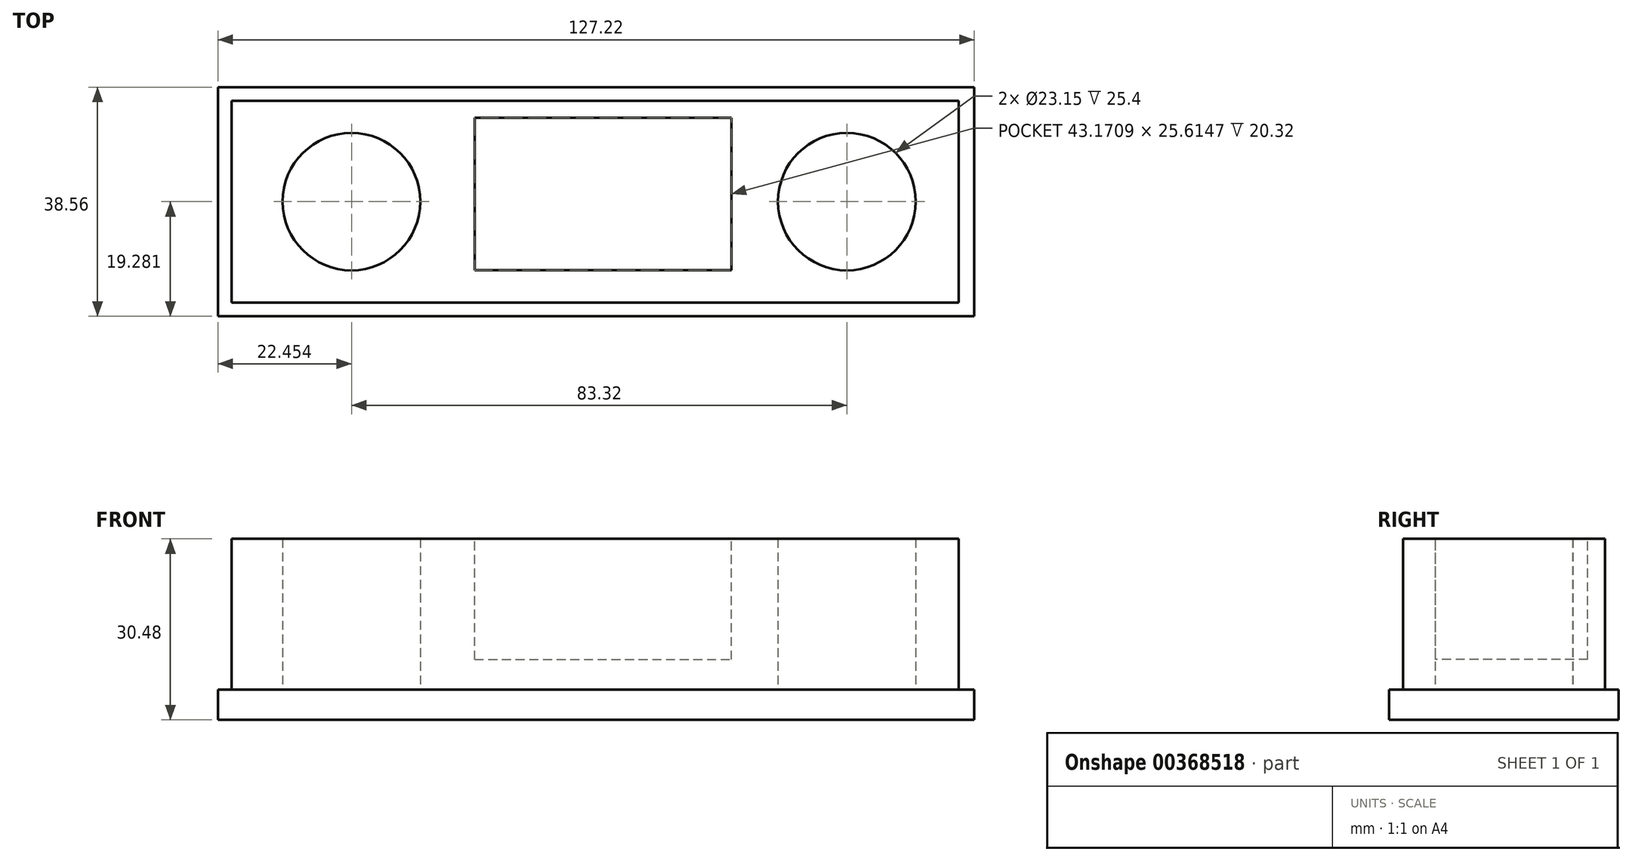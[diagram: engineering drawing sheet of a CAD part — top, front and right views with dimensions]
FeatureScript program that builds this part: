
annotation { "Feature Type Name" : "Feature", "Feature Type Description" : "" }
export const myFeature = defineFeature(function(context is Context, id is Id, definition is map)
    precondition{}
    {
        {
            var Q0;
            Q0=qCreatedBy(makeId("Top.planeOp"),FACE);
            var sketch = newSketch(context, id + "F0", { "sketchPlane" : qUnion([Q0])});
            skLineSegment(sketch, "E0.bottom", {"start": v(-63.6, 41.44) * mm, "end": v(63.6, 41.44) * mm});
            skLineSegment(sketch, "E0.top", {"start": v(-63.6, 2.88) * mm, "end": v(63.6, 2.88) * mm});
            skLineSegment(sketch, "E0.left", {"start": v(-63.6, 41.44) * mm, "end": v(-63.6, 2.88) * mm});
            skLineSegment(sketch, "E0.right", {"start": v(63.6, 41.44) * mm, "end": v(63.6, 2.88) * mm});
            skSolve(sketch);
        }
        {
            var Q0;
            Q0 = qSketchRegion(id + "F0", true);
            var Q1;
            Q1=makeQuery(id+"F0.imprint","IMPRINT",FACE,{"disambiguationData":[TD([[makeQuery(id+"F0.imprint","IMPRINT",EDGE,{"derivedFrom":sQuery(id+"F0.wireOp",EDGE,"E0.bottom")}),-1.0]])]});
            extrude(context, id + "F1", {"entities" : qUnion([Q0, Q1]), "oppositeDirection" : true, "depth" : 5.08 * mm});
        }
        {
            var Q0;
            Q0=makeQuery(id+"F1.opExtrude","CAP_FACE",FACE,{"disambiguationData":[OSD([sQuery(id+"F0.wireOp",EDGE,"E0.bottom"),sQuery(id+"F0.wireOp",EDGE,"E0.top"),sQuery(id+"F0.wireOp",EDGE,"E0.left"),sQuery(id+"F0.wireOp",EDGE,"E0.right")])],"isStart":true});
            var sketch = newSketch(context, id + "F2", { "sketchPlane" : qUnion([Q0])});
            skLineSegment(sketch, "E1.left", {"start": v(-61.3, 39.14) * mm, "end": v(-61.3, 5.18) * mm});
            skLineSegment(sketch, "E1.right", {"start": v(61.01, 39.14) * mm, "end": v(61.01, 5.18) * mm});
            skLineSegment(sketch, "E2.bottom", {"start": v(-63.6, 41.44) * mm, "end": v(-0.14, 41.44) * mm});
            skLineSegment(sketch, "E2.top", {"start": v(-63.6, 2.88) * mm, "end": v(-0.14, 2.88) * mm});
            skLineSegment(sketch, "E2.left", {"start": v(-63.6, 41.44) * mm, "end": v(-63.6, 2.88) * mm});
            skCircle(sketch, "E3", {"center": v(-41.16, 22.16) * mm, "radius": 11.58 * mm});
            skCircle(sketch, "E4", {"center": v(42.16, 22.16) * mm, "radius": 11.57 * mm});
            skLineSegment(sketch, "E5", {"start": v(-61.3, 39.14) * mm, "end": v(61.01, 39.14) * mm});
            skLineSegment(sketch, "E6", {"start": v(-61.3, 5.18) * mm, "end": v(61.01, 5.18) * mm});
            skSolve(sketch);
        }
        {
            var Q0;
            Q0=makeQuery(id+"F2.imprint","IMPRINT",FACE,{"disambiguationData":[TD([[makeQuery(id+"F2.imprint","IMPRINT",EDGE,{"derivedFrom":sQuery(id+"F2.wireOp",EDGE,"E1.left")}),1.0]])]});
            extrude(context, id + "F3", {"entities" : qUnion([Q0]), "operationType" : NewBodyOperationType.ADD, "depth" : 25.4 * mm});
        }
        {
            var Q0;
            Q0=makeQuery(id+"F3.opExtrude","CAP_FACE",FACE,{"disambiguationData":[OSD([sQuery(id+"F2.wireOp",EDGE,"E1.left"),sQuery(id+"F2.wireOp",EDGE,"E1.right"),sQuery(id+"F2.wireOp",EDGE,"E3"),sQuery(id+"F2.wireOp",EDGE,"E4"),sQuery(id+"F2.wireOp",EDGE,"E5"),sQuery(id+"F2.wireOp",EDGE,"E6")])],"isStart":false});
            var sketch = newSketch(context, id + "F4", { "sketchPlane" : qUnion([Q0])});
            skLineSegment(sketch, "E7.bottom", {"start": v(-0.14, 39.14) * mm, "end": v(21.59, 39.14) * mm});
            skLineSegment(sketch, "E7.top", {"start": v(-0.14, 5.18) * mm, "end": v(21.59, 5.18) * mm});
            skLineSegment(sketch, "E8.bottom", {"start": v(21.59, 39.14) * mm, "end": v(3.45, 39.14) * mm});
            skLineSegment(sketch, "E9.bottom", {"start": v(21.59, 39.14) * mm, "end": v(-21.59, 39.14) * mm});
            skLineSegment(sketch, "E9.top", {"start": v(21.59, 5.18) * mm, "end": v(-21.59, 5.18) * mm});
            skLineSegment(sketch, "E10.bottom", {"start": v(18.7, 39.14) * mm, "end": v(-20.15, 39.14) * mm});
            skLineSegment(sketch, "E10.top", {"start": v(20.72, 7.18) * mm, "end": v(-20.15, 7.18) * mm});
            skLineSegment(sketch, "E11", {"start": v(-20.15, 37.14) * mm, "end": v(20.72, 37.14) * mm});
            skLineSegment(sketch, "E12", {"start": v(-20.15, 37.14) * mm, "end": v(-20.15, 7.18) * mm});
            skLineSegment(sketch, "E13", {"start": v(20.72, 37.14) * mm, "end": v(20.72, 7.18) * mm});
            skSolve(sketch);
        }
        {
            var Q0;
            Q0 = qSketchRegion(id + "F4", true);
            extrude(context, id + "F5", {"entities" : qUnion([Q0]), "operationType" : NewBodyOperationType.ADD, "oppositeDirection" : true, "depth" : 22.86 * mm});
        }
        {
            var Q0;
            Q0=makeQuery(id+"F3.opExtrude","CAP_FACE",FACE,{"disambiguationData":[OSD([sQuery(id+"F2.wireOp",EDGE,"E1.left"),sQuery(id+"F2.wireOp",EDGE,"E1.right"),sQuery(id+"F2.wireOp",EDGE,"E3"),sQuery(id+"F2.wireOp",EDGE,"E4"),sQuery(id+"F2.wireOp",EDGE,"E5"),sQuery(id+"F2.wireOp",EDGE,"E6")])],"isStart":false});
            var sketch = newSketch(context, id + "F6", { "sketchPlane" : qUnion([Q0])});
            skLineSegment(sketch, "E14.bottom", {"start": v(-20.43, 36.26) * mm, "end": v(22.74, 36.26) * mm});
            skLineSegment(sketch, "E14.top", {"start": v(-20.43, 10.65) * mm, "end": v(22.74, 10.65) * mm});
            skLineSegment(sketch, "E14.left", {"start": v(-20.43, 36.26) * mm, "end": v(-20.43, 10.65) * mm});
            skLineSegment(sketch, "E14.right", {"start": v(22.74, 36.26) * mm, "end": v(22.74, 10.65) * mm});
            skSolve(sketch);
        }
        {
            var Q0;
            Q0=makeQuery(id+"F6.imprint","IMPRINT",FACE,{"disambiguationData":[TD([[makeQuery(id+"F6.imprint","IMPRINT",EDGE,{"derivedFrom":sQuery(id+"F6.wireOp",EDGE,"E14.bottom")}),-1.0]])]});
            extrude(context, id + "F7", {"entities" : qUnion([Q0]), "operationType" : NewBodyOperationType.REMOVE, "oppositeDirection" : true, "depth" : 20.32 * mm});
        }
    });
